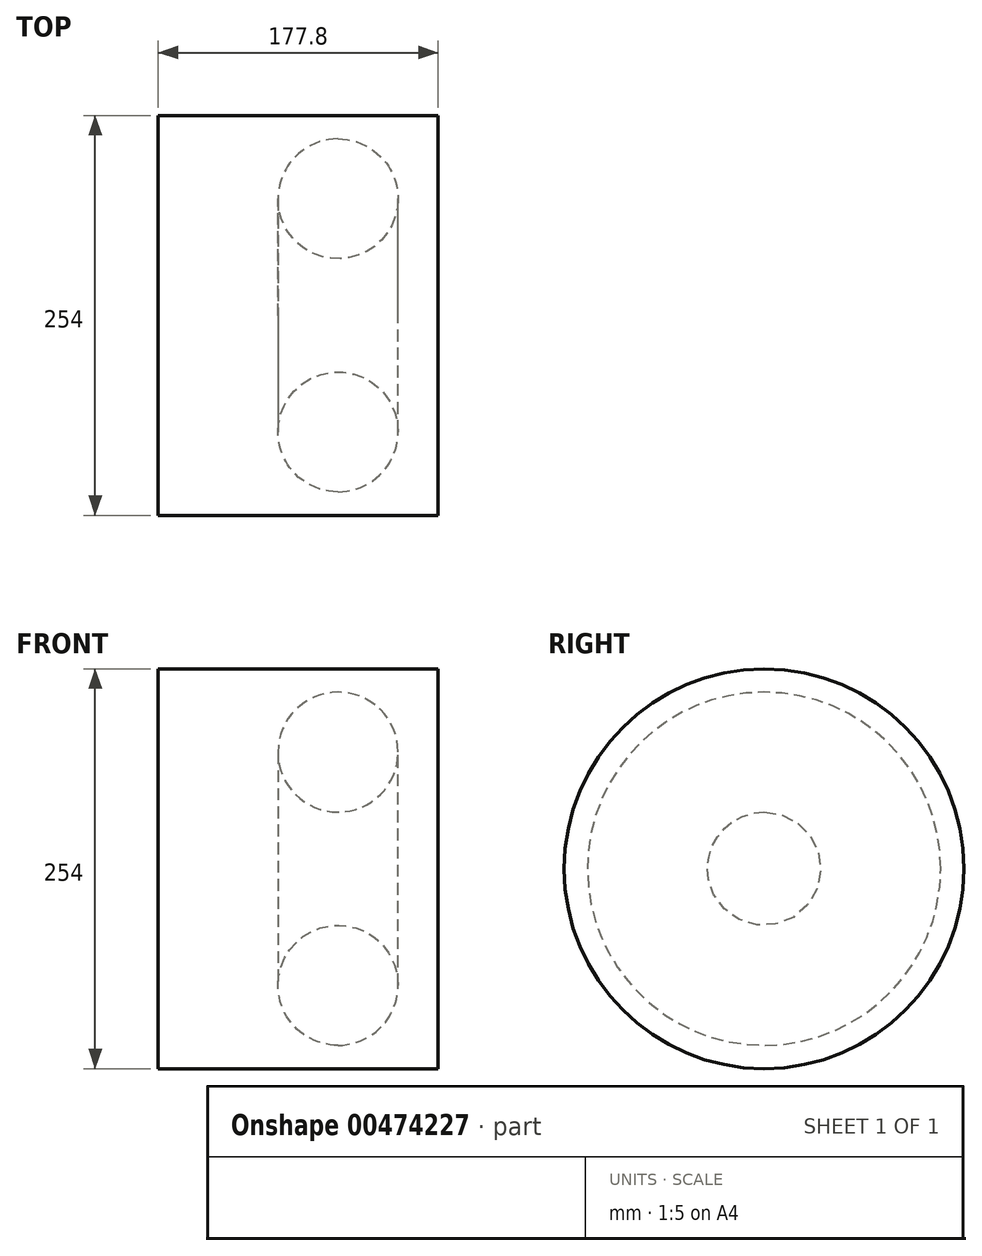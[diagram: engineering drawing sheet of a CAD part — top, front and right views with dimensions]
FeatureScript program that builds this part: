
annotation { "Feature Type Name" : "Feature", "Feature Type Description" : "" }
export const myFeature = defineFeature(function(context is Context, id is Id, definition is map)
    precondition{}
    {
        {
            var Q0;
            Q0=qCreatedBy(makeId("Top.planeOp"),FACE);
            var sketch = newSketch(context, id + "F0", { "sketchPlane" : qUnion([Q0])});
            skLineSegment(sketch, "E0.bottom", {"start": v(-62.77, 71.5) * mm, "end": v(115.03, 71.5) * mm});
            skLineSegment(sketch, "E0.top", {"start": v(-62.77, -55.5) * mm, "end": v(115.03, -55.5) * mm});
            skLineSegment(sketch, "E0.left", {"start": v(-62.77, 71.5) * mm, "end": v(-62.77, -55.5) * mm});
            skLineSegment(sketch, "E0.right", {"start": v(115.03, 71.5) * mm, "end": v(115.03, -55.5) * mm});
            skCircle(sketch, "E1", {"center": v(51.4, -2.55) * mm, "radius": 38.1 * mm});
            skSolve(sketch);
        }
        {
            var Q0;
            Q0 = qSketchRegion(id + "F0", true);
            var Q1;
            Q1=sQuery(id+"F0.wireOp",EDGE,"E0.bottom");
            revolve(context, id + "F1", {"entities" : qUnion([Q0]), "axis" : qUnion([Q1]), "revolveType" : RevolveType.FULL});
        }
    });
